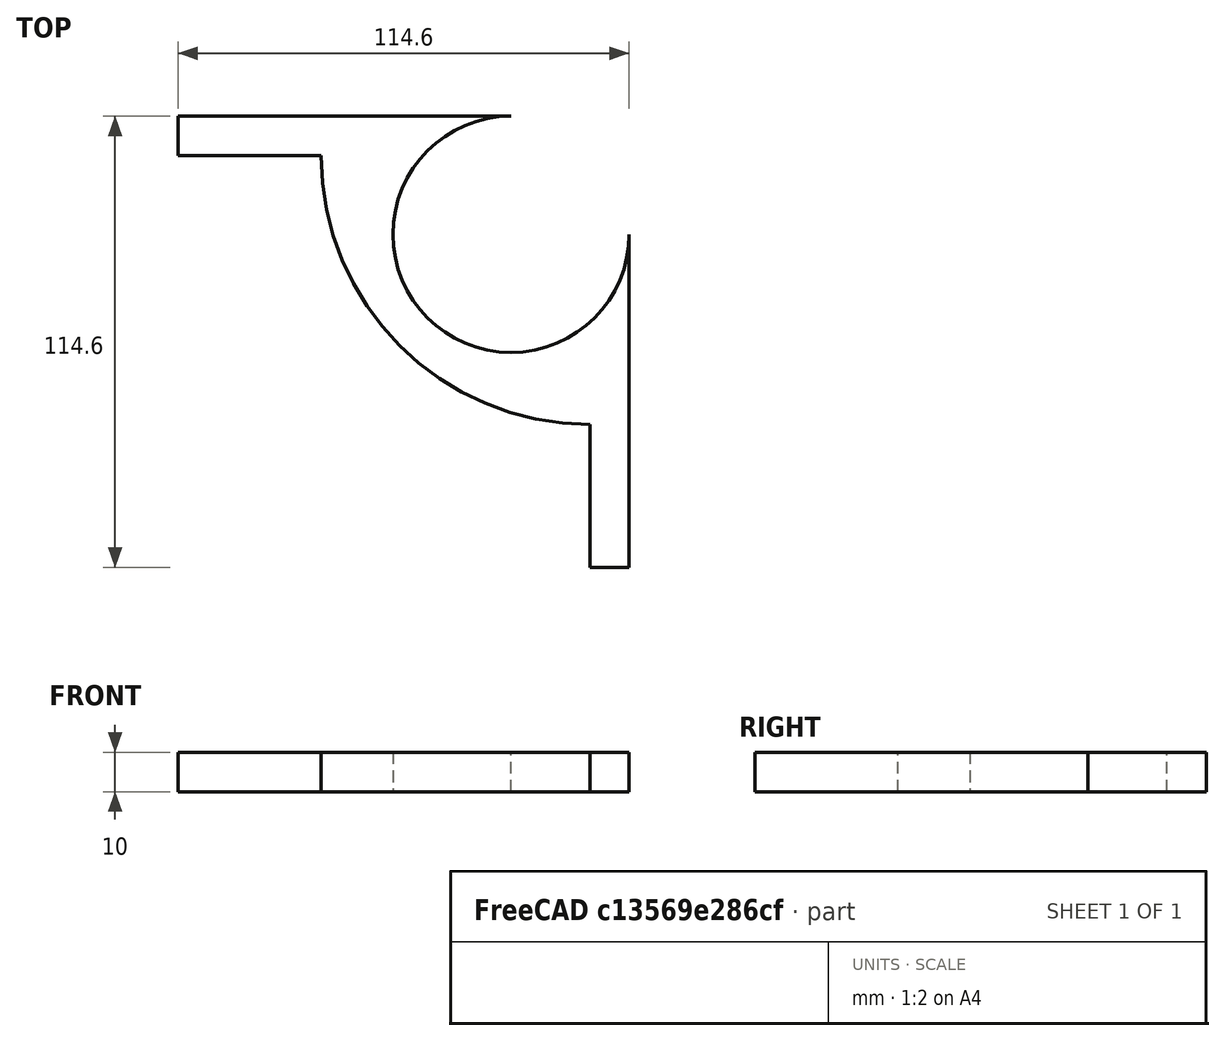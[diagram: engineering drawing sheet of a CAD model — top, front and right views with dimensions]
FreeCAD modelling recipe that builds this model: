
FCSTD DOCUMENT  (FreeCAD 0.22R38127 (Git))
Label: squirrel safe bird feeder pole upper
License: All rights reserved
LicenseURL: http://en.wikipedia.org/wiki/All_rights_reserved
objects: Sketcher::SketchObject×1, PartDesign::Pad×1, PartDesign::Body×1
note: 4 computed .brp shape members not serialized (recipe doc carries the construction recipe); baked Part::Feature solids carry a one-line shape summary decoded from their .brp

FEATURE [Sketcher::SketchObject] Sketch
  AttachmentSupport = -> [XY_Plane]
  FullyConstrained = false
  MapMode = 5
  sketch-geometry (11):
    g0: LineSegment StartX=-10 StartY=-114.602 StartZ=0 EndX=0 EndY=-114.602 EndZ=0
    g1: LineSegment StartX=-114.602 StartY=0 StartZ=0 EndX=-114.602 EndY=-10 EndZ=0
    g2: LineSegment StartX=-114.602 StartY=-10 StartZ=0 EndX=-78.2843 EndY=-10 EndZ=0
    g3: ArcOfCircle CenterX=-10 CenterY=-10 CenterZ=0 NormalX=0 NormalY=0 NormalZ=1 AngleXU=0 Radius=68.2843 StartAngle=3.14159 EndAngle=4.71239
    g4: ArcOfCircle CenterX=-30 CenterY=-30 CenterZ=0 NormalX=0 NormalY=0 NormalZ=1 AngleXU=0 Radius=30 StartAngle=1.5708 EndAngle=6.28319
    g5: LineSegment StartX=-30 StartY=0 StartZ=0 EndX=-114.602 EndY=-1.02787e-08 EndZ=0
    g6: LineSegment StartX=0 StartY=-30 StartZ=0 EndX=0 EndY=-114.602 EndZ=0
    g7: LineSegment StartX=-10 StartY=-78.2843 StartZ=0 EndX=-10 EndY=-114.602 EndZ=0
    g8: LineSegment StartX=0 StartY=0 StartZ=0 EndX=-132.175 EndY=-132.175 EndZ=0
    g9: GeomPoint X=-58.2843 Y=-58.2843 Z=0
    g10: GeomPoint X=-51.2132 Y=-51.2132 Z=0
  constraints (28):
    c: Horizontal(g0)
    c: PointOnObject(g1,g-1)
    c: Vertical(g1)
    c: Coincident(g1,g2)
    c: Horizontal(g2)
    c: Coincident(g2,g3)
    c: Radius(g4) = 30
    c: Coincident(g4,g5)
    c: Coincident(g3,g7)
    c: Vertical(g7)
    c: Coincident(g7,g0)
    c: Coincident(g0,g6)
    c: Tangent(g4,g-1) = 1.5708
    c: Tangent(g6,g-2)
    c: Tangent(g4,g6) = 1.5708
    c: Perpendicular(g3,g2)
    c: Perpendicular(g3,g7)
    c: Vertical(g1,g5)
    c: Equal(g2,g7)
    c: Equal(g6,g5)
    c: Coincident(g-1,g8)
    c: PointOnObject(g4,g8)
    c: PointOnObject(g9,g3)
    c: PointOnObject(g9,g8)
    c: PointOnObject(g10,g4)
    c: PointOnObject(g10,g8)
    c: Distance(g10,g9) = 10
    c: DistanceY(g1,g1) = 10
FEATURE [PartDesign::Pad] Pad
  Direction = (0,0,1)
  Length = 10
  Length2 = 10
  Profile = -> Sketch
  ReferenceAxis = -> Sketch [N_Axis]
  Suppressed = false
  Type = 0
FEATURE [PartDesign::Body] Body
  AllowCompound = false
  Group = -> [Sketch,Pad]
  Origin = -> Origin
  Tip = -> Pad
